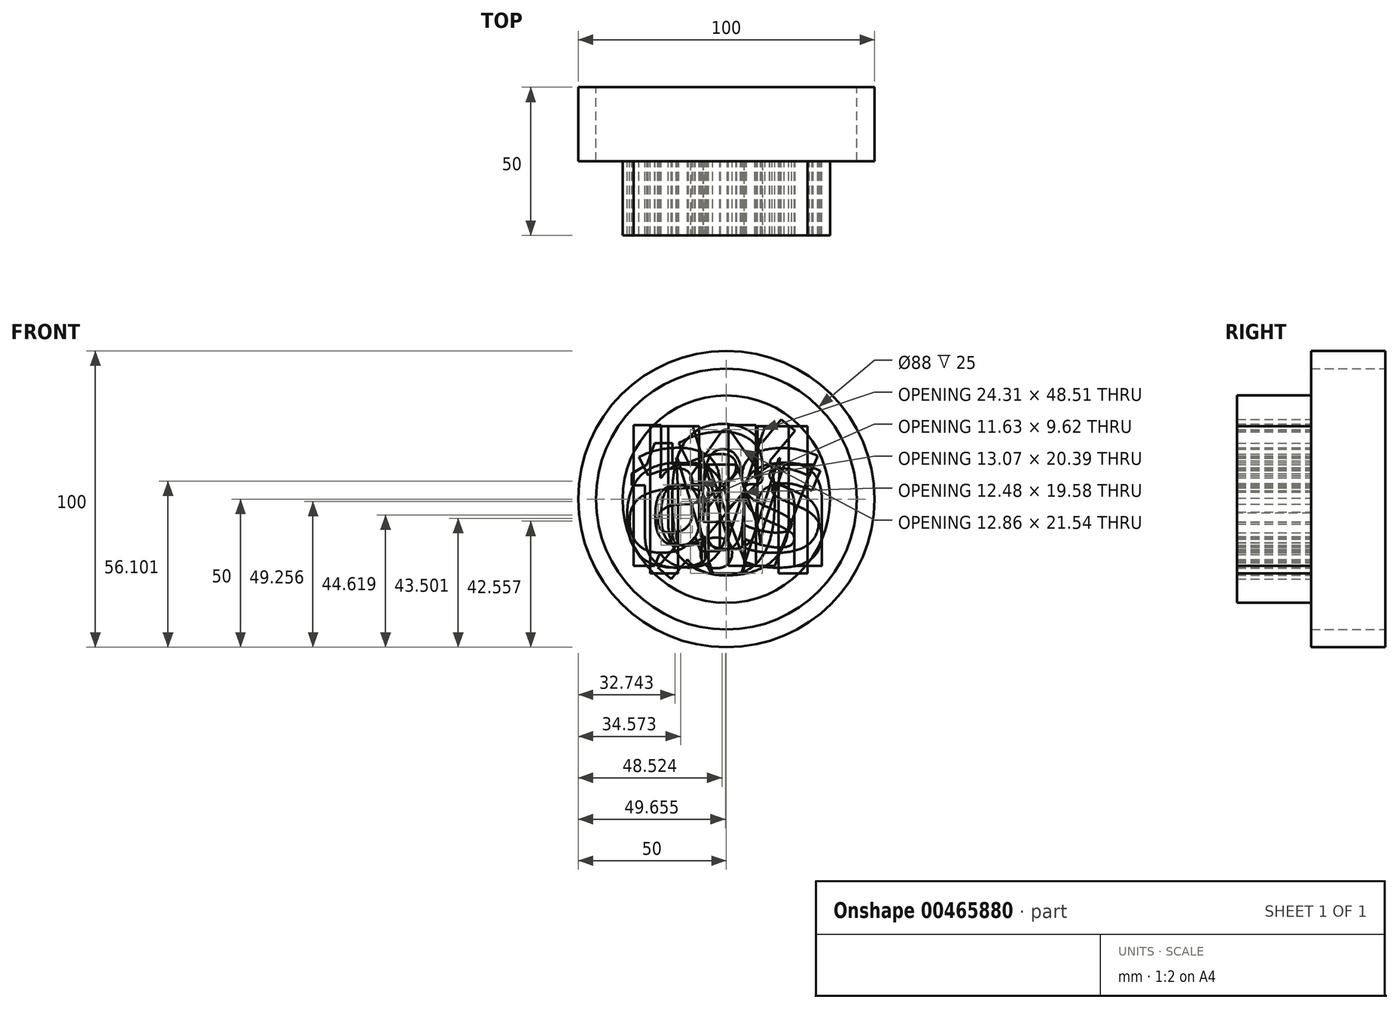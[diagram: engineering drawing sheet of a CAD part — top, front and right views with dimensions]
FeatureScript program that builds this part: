
annotation { "Feature Type Name" : "Feature", "Feature Type Description" : "" }
export const myFeature = defineFeature(function(context is Context, id is Id, definition is map)
    precondition{}
    {
        {
            var Q0;
            Q0=qCreatedBy(makeId("Front.planeOp"),FACE);
            var sketch = newSketch(context, id + "F0", { "sketchPlane" : qUnion([Q0])});
            skCircle(sketch, "E0", {"center": v(0, 0) * mm, "radius": 50 * mm});
            skCircle(sketch, "E1.0", {"center": v(0, 0) * mm, "radius": 44 * mm});
            skText(sketch, "E2", { "text": "as", "fontName": "OpenSans-Bold.ttf"});
            const initialGuessF0  = {"E2": [-0.0204, -0.00866, 1, 0, 0.02779]};
            skSetInitialGuess(sketch, initialGuessF0);
            skSolve(sketch);
        }
        {
            var Q0;
            Q0=makeQuery(id+"F0.imprint","IMPRINT",FACE,{"disambiguationData":[TD([[makeQuery(id+"F0.imprint","IMPRINT",EDGE,{"derivedFrom":sQuery(id+"F0.wireOp",EDGE,"E2.sketch_text.stroke-25")}),-1.0]])]});
            var Q1;
            Q1=makeQuery(id+"F0.imprint","IMPRINT",FACE,{"disambiguationData":[TD([[makeQuery(id+"F0.imprint","IMPRINT",EDGE,{"derivedFrom":sQuery(id+"F0.wireOp",EDGE,"E2.sketch_text.stroke-0")}),-1.0]])]});
            extrude(context, id + "F1", {"entities" : qUnion([Q0, Q1]), "depth" : 25 * mm});
        }
        {
            var Q0;
            Q0 = qSketchRegion(id + "F0", true);
            var Q1;
            Q1=makeQuery(id+"F0.imprint","IMPRINT",FACE,{"disambiguationData":[TD([[makeQuery(id+"F0.imprint","IMPRINT",EDGE,{"derivedFrom":sQuery(id+"F0.wireOp",EDGE,"E0")}),1.0]])]});
            extrude(context, id + "F2", {"entities" : qUnion([Q0, Q1]), "depth" : 25 * mm});
        }
        {
            var Q0;
            Q0=makeQuery(id+"F2.opExtrude","CAP_FACE",FACE,{"disambiguationData":[OSD([sQuery(id+"F0.wireOp",EDGE,"E0"),sQuery(id+"F0.wireOp",EDGE,"E1.0")])],"isStart":false});
            var sketch = newSketch(context, id + "F3", { "sketchPlane" : qUnion([Q0])});
            skText(sketch, "E3", { "text": "as", "fontName": "OpenSans-Bold.ttf"});
            skLineSegment(sketch, "E4", {"start": v(-35.25, 17.5) * mm, "end": v(35.25, 17.5) * mm});
            const initialGuessF3  = {"E3": [-0.03525, -0.0175, 1, 0, 0.045]};
            skSetInitialGuess(sketch, initialGuessF3);
            skSolve(sketch);
        }
        {
            var Q0;
            Q0=makeQuery(id+"F3.imprint","IMPRINT",FACE,{"disambiguationData":[TD([[makeQuery(id+"F3.imprint","IMPRINT",EDGE,{"derivedFrom":sQuery(id+"F3.wireOp",EDGE,"E3.sketch_text.stroke-0")}),-1.0]])]});
            var Q1;
            Q1=makeQuery(id+"F3.imprint","IMPRINT",FACE,{"disambiguationData":[TD([[makeQuery(id+"F3.imprint","IMPRINT",EDGE,{"derivedFrom":sQuery(id+"F3.wireOp",EDGE,"E3.sketch_text.stroke-25")}),-1.0]])]});
            extrude(context, id + "F4", {"entities" : qUnion([Q0, Q1]), "depth" : 25 * mm});
        }
        {
            var Q0;
            Q0=makeQuery(id+"F2.opExtrude","CAP_FACE",FACE,{"disambiguationData":[OSD([sQuery(id+"F0.wireOp",EDGE,"E0"),sQuery(id+"F0.wireOp",EDGE,"E1.0")])],"isStart":false});
            var sketch = newSketch(context, id + "F5", { "sketchPlane" : qUnion([Q0])});
            skText(sketch, "E5", { "text": "0", "fontName": "OpenSans-Bold.ttf"});
            skLineSegment(sketch, "E6", {"start": v(0, 0) * mm, "end": v(20.83, 25) * mm});
            skLineSegment(sketch, "E7", {"start": v(0, 0) * mm, "end": v(-20.83, -25) * mm});
            skLineSegment(sketch, "E8.0", {"start": v(2.3, -1.92) * mm, "end": v(23.14, 23.08) * mm});
            skLineSegment(sketch, "E9.0", {"start": v(-2.3, 1.92) * mm, "end": v(-23.14, -23.08) * mm});
            skLineSegment(sketch, "E10", {"start": v(-2.3, 1.92) * mm, "end": v(2.3, -1.92) * mm});
            skLineSegment(sketch, "E11", {"start": v(20.83, 25) * mm, "end": v(23.14, 23.08) * mm});
            skLineSegment(sketch, "E12", {"start": v(-23.14, -23.08) * mm, "end": v(-20.83, -25) * mm});
            skLineSegment(sketch, "E13", {"start": v(2.3, -1.92) * mm, "end": v(-18.53, -26.92) * mm});
            skLineSegment(sketch, "E14", {"start": v(-2.3, 1.92) * mm, "end": v(18.53, 26.92) * mm});
            skLineSegment(sketch, "E15", {"start": v(-20.83, -25) * mm, "end": v(-18.53, -26.92) * mm});
            skLineSegment(sketch, "E16", {"start": v(20.83, 25) * mm, "end": v(18.53, 26.92) * mm});
            const initialGuessF5  = {"E5": [-0.02083, -0.025, 1, 0, 0.05]};
            skSetInitialGuess(sketch, initialGuessF5);
            skSolve(sketch);
        }
        {
            var Q0;
            {var subQ0=sQuery(id+"F5.wireOp",EDGE,"E15");Q0=makeQuery(id+"F5.imprint","IMPRINT",FACE,{"disambiguationData":[TD([[makeQuery(id+"F5.imprint","IMPRINT",EDGE,{"derivedFrom":subQ0}),1.0]])]});}
            var Q1;
            {var subQ5=sQuery(id+"F5.wireOp",EDGE,"E12");Q1=makeQuery(id+"F5.imprint","IMPRINT",FACE,{"disambiguationData":[TD([[makeQuery(id+"F5.imprint","IMPRINT",EDGE,{"derivedFrom":subQ5}),1.0]])]});}
            var Q2;
            {var subQ0=sQuery(id+"F5.wireOp",EDGE,"E16");Q2=makeQuery(id+"F5.imprint","IMPRINT",FACE,{"disambiguationData":[TD([[makeQuery(id+"F5.imprint","IMPRINT",EDGE,{"derivedFrom":subQ0}),1.0]])]});}
            var Q3;
            {var subQ5=sQuery(id+"F5.wireOp",EDGE,"E11");Q3=makeQuery(id+"F5.imprint","IMPRINT",FACE,{"disambiguationData":[TD([[makeQuery(id+"F5.imprint","IMPRINT",EDGE,{"derivedFrom":subQ5}),-1.0]])]});}
            var Q4;
            {var subQ8=sQuery(id+"F5.wireOp",EDGE,"E5.sketch_text.stroke-0");Q4=makeQuery(id+"F5.imprint","IMPRINT",FACE,{"disambiguationData":[TD([[makeQuery(id+"F5.imprint","IMPRINT",EDGE,{"derivedFrom":subQ8}),-1.0]])]});}
            var Q5;
            {var subQ1=sQuery(id+"F5.wireOp",EDGE,"E5.sketch_text.stroke-3");var subQ7=sQuery(id+"F5.wireOp",EDGE,"E5.sketch_text.stroke-2");var subQ8=makeQuery(id+"F5.imprint","INTERSECT",VERTEX,{"derivedFrom":[subQ7,subQ1]});Q5=makeQuery(id+"F5.imprint","IMPRINT",FACE,{"disambiguationData":[TD([[makeQuery(id+"F5.imprint","IMPRINT",EDGE,{"disambiguationData":[TD([[subQ8,1.0]])],"derivedFrom":subQ7}),-1.0]])]});}
            var Q6;
            {var subQ0=sQuery(id+"F5.wireOp",EDGE,"E7");var subQ1=sQuery(id+"F5.wireOp",EDGE,"E5.sketch_text.stroke-3");var subQ2=makeQuery(id+"F5.imprint","INTERSECT",VERTEX,{"derivedFrom":[subQ1,subQ0]});Q6=makeQuery(id+"F5.imprint","IMPRINT",FACE,{"disambiguationData":[TD([[makeQuery(id+"F5.imprint","IMPRINT",EDGE,{"disambiguationData":[TD([[subQ2,-1.0]])],"derivedFrom":subQ1}),-1.0]])]});}
            var Q7;
            {var subQ1=sQuery(id+"F5.wireOp",EDGE,"E5.sketch_text.stroke-7");var subQ7=sQuery(id+"F5.wireOp",EDGE,"E5.sketch_text.stroke-6");var subQ8=makeQuery(id+"F5.imprint","INTERSECT",VERTEX,{"derivedFrom":[subQ7,subQ1]});Q7=makeQuery(id+"F5.imprint","IMPRINT",FACE,{"disambiguationData":[TD([[makeQuery(id+"F5.imprint","IMPRINT",EDGE,{"disambiguationData":[TD([[subQ8,1.0]])],"derivedFrom":subQ7}),-1.0]])]});}
            var Q8;
            {var subQ0=sQuery(id+"F5.wireOp",EDGE,"E6");var subQ1=sQuery(id+"F5.wireOp",EDGE,"E5.sketch_text.stroke-7");var subQ2=makeQuery(id+"F5.imprint","INTERSECT",VERTEX,{"derivedFrom":[subQ1,subQ0]});Q8=makeQuery(id+"F5.imprint","IMPRINT",FACE,{"disambiguationData":[TD([[makeQuery(id+"F5.imprint","IMPRINT",EDGE,{"disambiguationData":[TD([[subQ2,-1.0]])],"derivedFrom":subQ1}),-1.0]])]});}
            var Q9;
            {var subQ12=sQuery(id+"F5.wireOp",EDGE,"E5.sketch_text.stroke-4");Q9=makeQuery(id+"F5.imprint","IMPRINT",FACE,{"disambiguationData":[TD([[makeQuery(id+"F5.imprint","IMPRINT",EDGE,{"derivedFrom":subQ12}),-1.0]])]});}
            var Q10;
            {var subQ0=sQuery(id+"F5.wireOp",EDGE,"E6");var subQ1=sQuery(id+"F5.wireOp",EDGE,"E5.sketch_text.stroke-12");var subQ2=makeQuery(id+"F5.imprint","INTERSECT",VERTEX,{"derivedFrom":[subQ1,subQ0]});Q10=makeQuery(id+"F5.imprint","IMPRINT",FACE,{"disambiguationData":[TD([[makeQuery(id+"F5.imprint","IMPRINT",EDGE,{"disambiguationData":[TD([[subQ2,-1.0]])],"derivedFrom":subQ1}),1.0]])]});}
            var Q11;
            {var subQ0=sQuery(id+"F5.wireOp",EDGE,"E8.0");var subQ1=sQuery(id+"F5.wireOp",EDGE,"E5.sketch_text.stroke-12");var subQ2=makeQuery(id+"F5.imprint","INTERSECT",VERTEX,{"derivedFrom":[subQ1,subQ0]});Q11=makeQuery(id+"F5.imprint","IMPRINT",FACE,{"disambiguationData":[TD([[makeQuery(id+"F5.imprint","IMPRINT",EDGE,{"disambiguationData":[TD([[subQ2,-1.0]])],"derivedFrom":subQ1}),1.0]])]});}
            var Q12;
            {var subQ0=sQuery(id+"F5.wireOp",EDGE,"E9.0");var subQ1=sQuery(id+"F5.wireOp",EDGE,"E5.sketch_text.stroke-8");var subQ2=makeQuery(id+"F5.imprint","INTERSECT",VERTEX,{"derivedFrom":[subQ1,subQ0]});Q12=makeQuery(id+"F5.imprint","IMPRINT",FACE,{"disambiguationData":[TD([[makeQuery(id+"F5.imprint","IMPRINT",EDGE,{"disambiguationData":[TD([[subQ2,-1.0]])],"derivedFrom":subQ1}),1.0]])]});}
            var Q13;
            {var subQ0=sQuery(id+"F5.wireOp",EDGE,"E7");var subQ1=sQuery(id+"F5.wireOp",EDGE,"E5.sketch_text.stroke-8");var subQ2=makeQuery(id+"F5.imprint","INTERSECT",VERTEX,{"derivedFrom":[subQ1,subQ0]});Q13=makeQuery(id+"F5.imprint","IMPRINT",FACE,{"disambiguationData":[TD([[makeQuery(id+"F5.imprint","IMPRINT",EDGE,{"disambiguationData":[TD([[subQ2,-1.0]])],"derivedFrom":subQ1}),1.0]])]});}
            extrude(context, id + "F6", {"entities" : qUnion([Q0, Q1, Q2, Q3, Q4, Q5, Q6, Q7, Q8, Q9, Q10, Q11, Q12, Q13]), "depth" : 25 * mm});
        }
        {
            var Q0;
            Q0=makeQuery(id+"F2.opExtrude","CAP_FACE",FACE,{"disambiguationData":[OSD([sQuery(id+"F0.wireOp",EDGE,"E0"),sQuery(id+"F0.wireOp",EDGE,"E1.0")])],"isStart":false});
            var sketch = newSketch(context, id + "F7", { "sketchPlane" : qUnion([Q0])});
            skText(sketch, "E17", { "text": "M", "fontName": "OpenSans-Bold.ttf"});
            const initialGuessF7  = {"E17": [-0.03187, -0.025, 1, 0, 0.05]};
            skSetInitialGuess(sketch, initialGuessF7);
            skSolve(sketch);
        }
        {
            var Q0;
            Q0=makeQuery(id+"F7.imprint","IMPRINT",FACE,{"disambiguationData":[TD([[makeQuery(id+"F7.imprint","IMPRINT",EDGE,{"derivedFrom":sQuery(id+"F7.wireOp",EDGE,"E17.sketch_text.stroke-0")}),-1.0]])]});
            extrude(context, id + "F8", {"entities" : qUnion([Q0]), "depth" : 25 * mm});
        }
        {
            var Q0;
            Q0=makeQuery(id+"F2.opExtrude","CAP_FACE",FACE,{"disambiguationData":[OSD([sQuery(id+"F0.wireOp",EDGE,"E0"),sQuery(id+"F0.wireOp",EDGE,"E1.0")])],"isStart":false});
            var sketch = newSketch(context, id + "F9", { "sketchPlane" : qUnion([Q0])});
            skText(sketch, "E18", { "text": "U", "fontName": "OpenSans-Bold.ttf"});
            const initialGuessF9  = {"E18": [-0.02555, -0.025, 1, 0, 0.05]};
            skSetInitialGuess(sketch, initialGuessF9);
            skSolve(sketch);
        }
        {
            var Q0;
            Q0 = qSketchRegion(id + "F9", true);
            extrude(context, id + "F10", {"entities" : qUnion([Q0]), "depth" : 25 * mm});
        }
        {
            var Q0;
            Q0=makeQuery(id+"F2.opExtrude","CAP_FACE",FACE,{"disambiguationData":[OSD([sQuery(id+"F0.wireOp",EDGE,"E0"),sQuery(id+"F0.wireOp",EDGE,"E1.0")])],"isStart":false});
            var sketch = newSketch(context, id + "F11", { "sketchPlane" : qUnion([Q0])});
            skText(sketch, "E19", { "text": "ch", "fontName": "OpenSans-Bold.ttf"});
            const initialGuessF11  = {"E19": [-0.03628, -0.0225, 1, 0, 0.045]};
            skSetInitialGuess(sketch, initialGuessF11);
            skSolve(sketch);
        }
        {
            var Q0;
            Q0=makeQuery(id+"F11.imprint","IMPRINT",FACE,{"disambiguationData":[TD([[makeQuery(id+"F11.imprint","IMPRINT",EDGE,{"derivedFrom":sQuery(id+"F11.wireOp",EDGE,"E19.sketch_text.stroke-0")}),-1.0]])]});
            var Q1;
            Q1=makeQuery(id+"F11.imprint","IMPRINT",FACE,{"disambiguationData":[TD([[makeQuery(id+"F11.imprint","IMPRINT",EDGE,{"derivedFrom":sQuery(id+"F11.wireOp",EDGE,"E19.sketch_text.stroke-14")}),-1.0]])]});
            extrude(context, id + "F12", {"entities" : qUnion([Q0, Q1]), "depth" : 25 * mm});
        }
        {
            var Q0;
            Q0=makeQuery(id+"F2.opExtrude","CAP_FACE",FACE,{"disambiguationData":[OSD([sQuery(id+"F0.wireOp",EDGE,"E0"),sQuery(id+"F0.wireOp",EDGE,"E1.0")])],"isStart":false});
            var sketch = newSketch(context, id + "F13", { "sketchPlane" : qUnion([Q0])});
            skText(sketch, "E20", { "text": "tv", "fontName": "OpenSans-Bold.ttf"});
            const initialGuessF13  = {"E20": [-0.03337, -0.0225, 1, 0, 0.045]};
            skSetInitialGuess(sketch, initialGuessF13);
            skSolve(sketch);
        }
        {
            var Q0;
            Q0=makeQuery(id+"F13.imprint","IMPRINT",FACE,{"disambiguationData":[TD([[makeQuery(id+"F13.imprint","IMPRINT",EDGE,{"derivedFrom":sQuery(id+"F13.wireOp",EDGE,"E20.sketch_text.stroke-0")}),-1.0]])]});
            var Q1;
            Q1=makeQuery(id+"F13.imprint","IMPRINT",FACE,{"disambiguationData":[TD([[makeQuery(id+"F13.imprint","IMPRINT",EDGE,{"derivedFrom":sQuery(id+"F13.wireOp",EDGE,"E20.sketch_text.stroke-18")}),-1.0]])]});
            extrude(context, id + "F14", {"entities" : qUnion([Q0, Q1]), "depth" : 25 * mm});
        }
        {
            var Q0;
            Q0=makeQuery(id+"F2.opExtrude","CAP_FACE",FACE,{"disambiguationData":[OSD([sQuery(id+"F0.wireOp",EDGE,"E0"),sQuery(id+"F0.wireOp",EDGE,"E1.0")])],"isStart":false});
            var sketch = newSketch(context, id + "F15", { "sketchPlane" : qUnion([Q0])});
            skText(sketch, "E21", { "text": "bs", "fontName": "OpenSans-Bold.ttf"});
            const initialGuessF15  = {"E21": [-0.03615, -0.0225, 1, 0, 0.045]};
            skSetInitialGuess(sketch, initialGuessF15);
            skSolve(sketch);
        }
        {
            var Q0;
            Q0=makeQuery(id+"F15.imprint","IMPRINT",FACE,{"disambiguationData":[TD([[makeQuery(id+"F15.imprint","IMPRINT",EDGE,{"derivedFrom":sQuery(id+"F15.wireOp",EDGE,"E21.sketch_text.stroke-0")}),-1.0]])]});
            var Q1;
            Q1=makeQuery(id+"F15.imprint","IMPRINT",FACE,{"disambiguationData":[TD([[makeQuery(id+"F15.imprint","IMPRINT",EDGE,{"derivedFrom":sQuery(id+"F15.wireOp",EDGE,"E21.sketch_text.stroke-23")}),-1.0]])]});
            extrude(context, id + "F16", {"entities" : qUnion([Q0, Q1]), "depth" : 25 * mm});
        }
        {
            var Q0;
            Q0=makeQuery(id+"F1.opExtrude","SWEPT_BODY",BODY,{"disambiguationData":[OSD([sQuery(id+"F0.wireOp",EDGE,"E2.sketch_text.stroke-0"),sQuery(id+"F0.wireOp",EDGE,"E2.sketch_text.stroke-1"),sQuery(id+"F0.wireOp",EDGE,"E2.sketch_text.stroke-2"),sQuery(id+"F0.wireOp",EDGE,"E2.sketch_text.stroke-3"),sQuery(id+"F0.wireOp",EDGE,"E2.sketch_text.stroke-4"),sQuery(id+"F0.wireOp",EDGE,"E2.sketch_text.stroke-5"),sQuery(id+"F0.wireOp",EDGE,"E2.sketch_text.stroke-6"),sQuery(id+"F0.wireOp",EDGE,"E2.sketch_text.stroke-7"),sQuery(id+"F0.wireOp",EDGE,"E2.sketch_text.stroke-8"),sQuery(id+"F0.wireOp",EDGE,"E2.sketch_text.stroke-9"),sQuery(id+"F0.wireOp",EDGE,"E2.sketch_text.stroke-10"),sQuery(id+"F0.wireOp",EDGE,"E2.sketch_text.stroke-11"),sQuery(id+"F0.wireOp",EDGE,"E2.sketch_text.stroke-12"),sQuery(id+"F0.wireOp",EDGE,"E2.sketch_text.stroke-13"),sQuery(id+"F0.wireOp",EDGE,"E2.sketch_text.stroke-14"),sQuery(id+"F0.wireOp",EDGE,"E2.sketch_text.stroke-15"),sQuery(id+"F0.wireOp",EDGE,"E2.sketch_text.stroke-16"),sQuery(id+"F0.wireOp",EDGE,"E2.sketch_text.stroke-17"),sQuery(id+"F0.wireOp",EDGE,"E2.sketch_text.stroke-18"),sQuery(id+"F0.wireOp",EDGE,"E2.sketch_text.stroke-19"),sQuery(id+"F0.wireOp",EDGE,"E2.sketch_text.stroke-20"),sQuery(id+"F0.wireOp",EDGE,"E2.sketch_text.stroke-21"),sQuery(id+"F0.wireOp",EDGE,"E2.sketch_text.stroke-22"),sQuery(id+"F0.wireOp",EDGE,"E2.sketch_text.stroke-23"),sQuery(id+"F0.wireOp",EDGE,"E2.sketch_text.stroke-24")])]});
            var Q1;
            Q1=makeQuery(id+"F1.opExtrude","SWEPT_BODY",BODY,{"disambiguationData":[OSD([sQuery(id+"F0.wireOp",EDGE,"E2.sketch_text.stroke-25"),sQuery(id+"F0.wireOp",EDGE,"E2.sketch_text.stroke-26"),sQuery(id+"F0.wireOp",EDGE,"E2.sketch_text.stroke-27"),sQuery(id+"F0.wireOp",EDGE,"E2.sketch_text.stroke-28"),sQuery(id+"F0.wireOp",EDGE,"E2.sketch_text.stroke-29"),sQuery(id+"F0.wireOp",EDGE,"E2.sketch_text.stroke-30"),sQuery(id+"F0.wireOp",EDGE,"E2.sketch_text.stroke-31"),sQuery(id+"F0.wireOp",EDGE,"E2.sketch_text.stroke-32"),sQuery(id+"F0.wireOp",EDGE,"E2.sketch_text.stroke-33"),sQuery(id+"F0.wireOp",EDGE,"E2.sketch_text.stroke-34"),sQuery(id+"F0.wireOp",EDGE,"E2.sketch_text.stroke-35"),sQuery(id+"F0.wireOp",EDGE,"E2.sketch_text.stroke-36"),sQuery(id+"F0.wireOp",EDGE,"E2.sketch_text.stroke-37"),sQuery(id+"F0.wireOp",EDGE,"E2.sketch_text.stroke-38"),sQuery(id+"F0.wireOp",EDGE,"E2.sketch_text.stroke-39"),sQuery(id+"F0.wireOp",EDGE,"E2.sketch_text.stroke-40"),sQuery(id+"F0.wireOp",EDGE,"E2.sketch_text.stroke-41"),sQuery(id+"F0.wireOp",EDGE,"E2.sketch_text.stroke-42"),sQuery(id+"F0.wireOp",EDGE,"E2.sketch_text.stroke-43"),sQuery(id+"F0.wireOp",EDGE,"E2.sketch_text.stroke-44"),sQuery(id+"F0.wireOp",EDGE,"E2.sketch_text.stroke-45"),sQuery(id+"F0.wireOp",EDGE,"E2.sketch_text.stroke-46"),sQuery(id+"F0.wireOp",EDGE,"E2.sketch_text.stroke-47"),sQuery(id+"F0.wireOp",EDGE,"E2.sketch_text.stroke-48"),sQuery(id+"F0.wireOp",EDGE,"E2.sketch_text.stroke-49"),sQuery(id+"F0.wireOp",EDGE,"E2.sketch_text.stroke-50")])]});
            deleteBodies(context, id + "F17", {"entities" : qUnion([Q0, Q1])});
        }
        {
            var Q0;
            Q0=makeQuery(id+"F2.opExtrude","CAP_FACE",FACE,{"disambiguationData":[OSD([sQuery(id+"F0.wireOp",EDGE,"E0"),sQuery(id+"F0.wireOp",EDGE,"E1.0")])],"isStart":false});
            var sketch = newSketch(context, id + "F18", { "sketchPlane" : qUnion([Q0])});
            skText(sketch, "E22", { "text": "?", "fontName": "OpenSans-Bold.ttf"});
            const initialGuessF18  = {"E22": [-0.01619, -0.0225, 1, 0, 0.045]};
            skSetInitialGuess(sketch, initialGuessF18);
            skSolve(sketch);
        }
        {
            var Q0;
            Q0=makeQuery(id+"F18.imprint","IMPRINT",FACE,{"disambiguationData":[TD([[makeQuery(id+"F18.imprint","IMPRINT",EDGE,{"derivedFrom":sQuery(id+"F18.wireOp",EDGE,"E22.sketch_text.stroke-0")}),-1.0]])]});
            var Q1;
            Q1=makeQuery(id+"F18.imprint","IMPRINT",FACE,{"disambiguationData":[TD([[makeQuery(id+"F18.imprint","IMPRINT",EDGE,{"derivedFrom":sQuery(id+"F18.wireOp",EDGE,"E22.sketch_text.stroke-18")}),-1.0]])]});
            extrude(context, id + "F19", {"entities" : qUnion([Q0, Q1]), "depth" : 25 * mm});
        }
        {
            var Q0;
            Q0=makeQuery(id+"F2.opExtrude","CAP_FACE",FACE,{"disambiguationData":[OSD([sQuery(id+"F0.wireOp",EDGE,"E0"),sQuery(id+"F0.wireOp",EDGE,"E1.0")])],"isStart":false});
            var sketch = newSketch(context, id + "F20", { "sketchPlane" : qUnion([Q0])});
            skCircle(sketch, "E23", {"center": v(0, 0) * mm, "radius": 35 * mm});
            skLineSegment(sketch, "E24", {"start": v(0, 25) * mm, "end": v(-14, 5) * mm});
            skLineSegment(sketch, "E25", {"start": v(-14, 5) * mm, "end": v(-6, 5) * mm});
            skLineSegment(sketch, "E26", {"start": v(-6, 5) * mm, "end": v(-6, -25) * mm});
            skLineSegment(sketch, "E27", {"start": v(-6, -25) * mm, "end": v(0, -25) * mm});
            skLineSegment(sketch, "E28", {"start": v(0, -25) * mm, "end": v(0, 25) * mm});
            skLineSegment(sketch, "E29.MirrorCS", {"start": v(6, 5) * mm, "end": v(6, -25) * mm});
            skLineSegment(sketch, "E30.MirrorCS", {"start": v(14, 5) * mm, "end": v(6, 5) * mm});
            skLineSegment(sketch, "E31.MirrorCS", {"start": v(0, 25) * mm, "end": v(14, 5) * mm});
            skLineSegment(sketch, "E32.MirrorCS", {"start": v(6, -25) * mm, "end": v(0, -25) * mm});
            skSolve(sketch);
        }
        {
            var Q0;
            Q0=makeQuery(id+"F20.imprint","IMPRINT",FACE,{"disambiguationData":[TD([[makeQuery(id+"F20.imprint","IMPRINT",EDGE,{"derivedFrom":sQuery(id+"F20.wireOp",EDGE,"E23")}),1.0]])]});
            extrude(context, id + "F21", {"entities" : qUnion([Q0]), "depth" : 25 * mm});
        }
        {
            var Q0;
            Q0=makeQuery(id+"F21.opExtrude","SWEPT_EDGE",EDGE,{"disambiguationData":[OSD([sQuery(id+"F20.wireOp",EDGE,"E24"),sQuery(id+"F20.wireOp",EDGE,"E25")])]});
            var Q1;
            Q1=makeQuery(id+"F21.opExtrude","SWEPT_EDGE",EDGE,{"disambiguationData":[OSD([sQuery(id+"F20.wireOp",EDGE,"E25"),sQuery(id+"F20.wireOp",EDGE,"E26")])]});
            var Q2;
            Q2=makeQuery(id+"F21.opExtrude","SWEPT_EDGE",EDGE,{"disambiguationData":[OSD([sQuery(id+"F20.wireOp",EDGE,"E26"),sQuery(id+"F20.wireOp",EDGE,"E27")])]});
            var Q3;
            Q3=makeQuery(id+"F21.opExtrude","SWEPT_EDGE",EDGE,{"disambiguationData":[OSD([sQuery(id+"F20.wireOp",EDGE,"E29.MirrorCS"),sQuery(id+"F20.wireOp",EDGE,"E32.MirrorCS")])]});
            var Q4;
            Q4=makeQuery(id+"F21.opExtrude","SWEPT_EDGE",EDGE,{"disambiguationData":[OSD([sQuery(id+"F20.wireOp",EDGE,"E29.MirrorCS"),sQuery(id+"F20.wireOp",EDGE,"E30.MirrorCS")])]});
            var Q5;
            Q5=makeQuery(id+"F21.opExtrude","SWEPT_EDGE",EDGE,{"disambiguationData":[OSD([sQuery(id+"F20.wireOp",EDGE,"E30.MirrorCS"),sQuery(id+"F20.wireOp",EDGE,"E31.MirrorCS")])]});
            var Q6;
            Q6=makeQuery(id+"F21.opExtrude","SWEPT_EDGE",EDGE,{"disambiguationData":[OSD([sQuery(id+"F20.wireOp",EDGE,"E24"),sQuery(id+"F20.wireOp",EDGE,"E28"),sQuery(id+"F20.wireOp",EDGE,"E31.MirrorCS")])]});
            fillet(context, id + "F22", {"entities" : qUnion([Q0, Q1, Q2, Q3, Q4, Q5, Q6]), "radius" : 2 * mm, "tangentPropagation" : true, "allowEdgeOverflow" : false});
        }
    });
